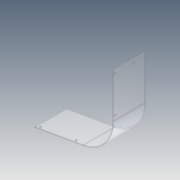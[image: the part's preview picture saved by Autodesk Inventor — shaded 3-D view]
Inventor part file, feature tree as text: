
AUTODESK INVENTOR PART (.ipt)
format: ipt  version: 2012 (Build 160160000, 160)  size: 95,744 bytes
history: native  units: in
note: dims shown in document units (in); Inventor stores cm internally (conversion verified against a paired STEP export)
features: pattern_linear x3, hole x2, extrude x1, sketch x1, reference x1
ambient origin geometry x8: Origin, YZ Plane, XZ Plane, XY Plane, X Axis, Y Axis, Z Axis, Center Point
bodies: Solid1 (feature_tree)
feature tree (8):
  extrude  "Extrusion1"  Depth=0.3125in
  hole  "Hole1"  [1 undecoded]
  pattern_linear  "Rectangular Pattern1"  Count1=2 Spacing1=5.25in
  pattern_linear  "Rectangular Pattern2"  Spacing1=0.5in  [1 undecoded]
  hole  "Hole2"  [1 undecoded]
  pattern_linear  "Rectangular Pattern3"  [2 undecoded]
  sketch  "Sketch1"  dims[d0=4.625in d1=0.0in d2=0.3125in d3=0.5in d4=0.265in d5=0.75in d6=0.375in d7=0.25in d8=0.5635in d9=1.0in d10=0.8108in d11=0.7874in d13=2.6875in d14=0.7874in d16=5.25in d17=0.5in d18=0.3125in d19=0.265in d20=0.75in d21=0.375in d22=0.25in d23=0.5635in d24=1.0in d25=0.8108in d26=0.7874in d28=5.25in]
  reference  "Reference1"
note: 5 required parameter values undecoded (feature->parameter linkage not recoverable at this tier; creation-order binding heuristic only, values carry confidence <= 0.55)
